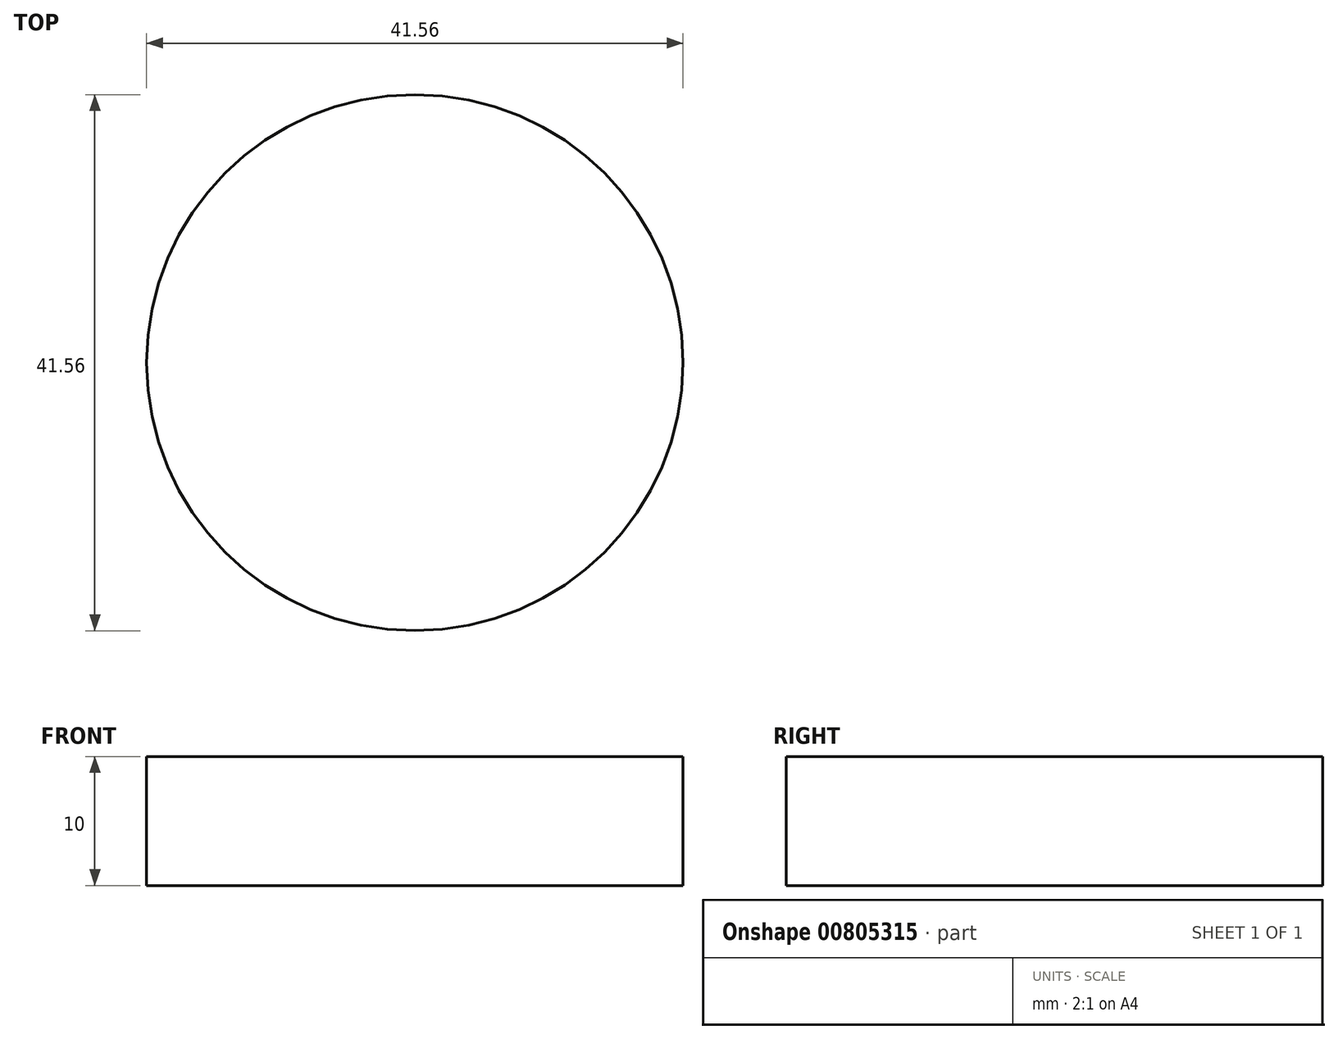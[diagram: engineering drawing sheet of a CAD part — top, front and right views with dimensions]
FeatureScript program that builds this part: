
annotation { "Feature Type Name" : "Feature", "Feature Type Description" : "" }
export const myFeature = defineFeature(function(context is Context, id is Id, definition is map)
    precondition{}
    {
        {
            var Q0;
            Q0=qCreatedBy(makeId("Top.planeOp"),FACE);
            var sketch = newSketch(context, id + "F0", { "sketchPlane" : qUnion([Q0])});
            skCircle(sketch, "E0", {"center": v(-28.67, -9.09) * mm, "radius": 20.78 * mm});
            skSolve(sketch);
        }
        {
            var Q0;
            Q0 = qSketchRegion(id + "F0", true);
            extrude(context, id + "F1", {"entities" : qUnion([Q0]), "depth" : 10 * mm, "offsetDistance" : 25 * mm});
        }
    });
